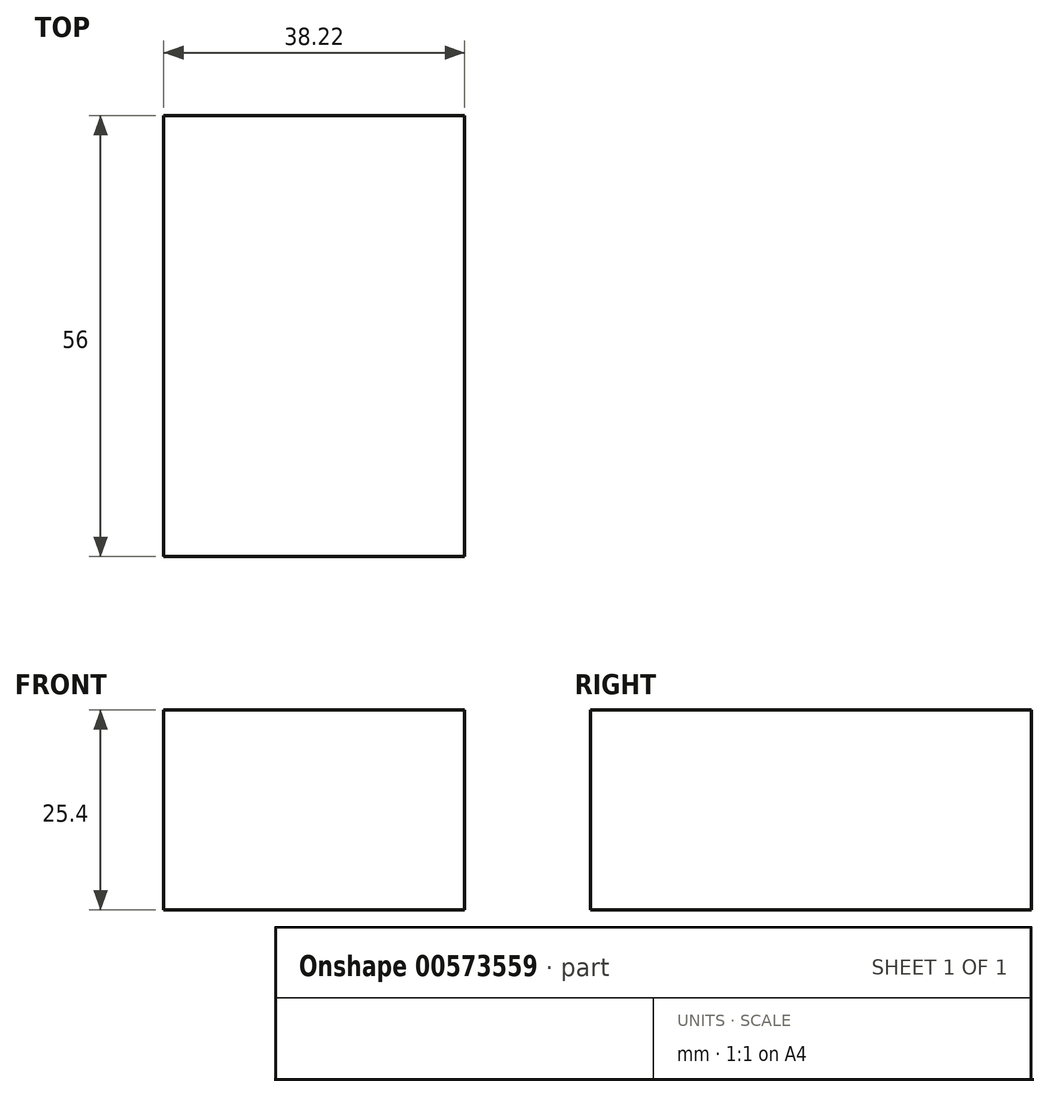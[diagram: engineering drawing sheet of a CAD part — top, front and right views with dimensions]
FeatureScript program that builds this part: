
annotation { "Feature Type Name" : "Feature", "Feature Type Description" : "" }
export const myFeature = defineFeature(function(context is Context, id is Id, definition is map)
    precondition{}
    {
        {
            var Q0;
            Q0=qCreatedBy(makeId("Top.planeOp"),FACE);
            var sketch = newSketch(context, id + "F0", { "sketchPlane" : qUnion([Q0])});
            skLineSegment(sketch, "E0.bottom", {"start": v(7.33, 13.6) * mm, "end": v(-30.9, 13.6) * mm});
            skLineSegment(sketch, "E0.top", {"start": v(7.33, -42.4) * mm, "end": v(-30.9, -42.4) * mm});
            skLineSegment(sketch, "E0.left", {"start": v(7.33, 13.6) * mm, "end": v(7.33, -42.4) * mm});
            skLineSegment(sketch, "E0.right", {"start": v(-30.9, 13.6) * mm, "end": v(-30.9, -42.4) * mm});
            skSolve(sketch);
        }
        {
            var Q0;
            Q0 = qSketchRegion(id + "F0", true);
            extrude(context, id + "F1", {"entities" : qUnion([Q0]), "depth" : 25.4 * mm, "offsetDistance" : 25.4 * mm});
        }
    });
